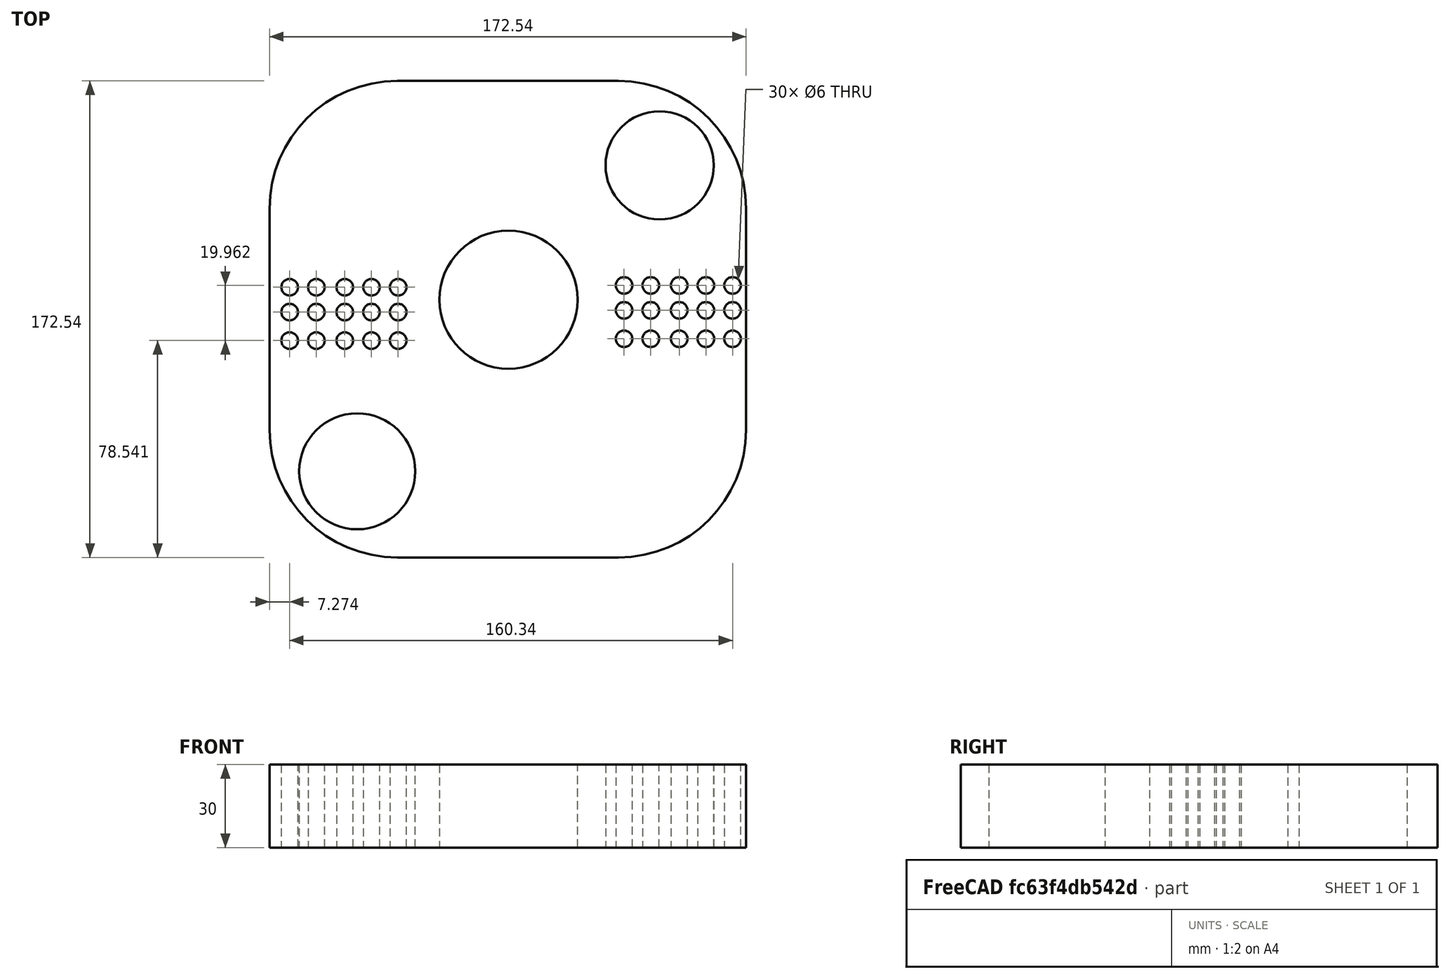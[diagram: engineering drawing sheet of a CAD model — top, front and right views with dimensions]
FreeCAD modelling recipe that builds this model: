
FCSTD DOCUMENT  (FreeCAD 0.18R16131 (Git))
Label: Momentum_Mold_Plate_1-2_160X200_12T_25mm(lm12uu) (2)
License: All rights reserved
LicenseURL: http://en.wikipedia.org/wiki/All_rights_reserved
objects: PartDesign::Pad×2, Sketcher::SketchObject×1, PartDesign::Body×1
note: 6 computed .brp shape members not serialized (recipe doc carries the construction recipe); baked Part::Feature solids carry a one-line shape summary decoded from their .brp

FEATURE [Sketcher::SketchObject] Sketch
  MapMode = 5
  Support = -> [XY_Plane]
  sketch-geometry (41):
    g0: LineSegment StartX=-35.5842 StartY=-63.1111 StartZ=0 EndX=44.4158 EndY=-63.1111 EndZ=0
    g1: LineSegment StartX=90.685 StartY=-16.8419 StartZ=0 EndX=90.685 EndY=63.1581 EndZ=0
    g2: LineSegment StartX=44.4158 StartY=109.427 StartZ=0 EndX=-35.5842 EndY=109.427 EndZ=0
    g3: LineSegment StartX=-81.8534 StartY=63.1581 StartZ=0 EndX=-81.8534 EndY=-16.8419 EndZ=0
    g4: Circle CenterX=4.62833 CenterY=30.2412 CenterZ=0 NormalX=0 NormalY=0 NormalZ=1 AngleXU=0 Radius=25
    g5: Circle CenterX=-50.1062 CenterY=-31.8986 CenterZ=0 NormalX=0 NormalY=0 NormalZ=1 AngleXU=0 Radius=21
    g6: Circle CenterX=59.3629 CenterY=78.8583 CenterZ=0 NormalX=0 NormalY=0 NormalZ=1 AngleXU=0 Radius=19.5845
    g7: ArcOfCircle CenterX=-35.5842 CenterY=63.1581 CenterZ=0 NormalX=0 NormalY=0 NormalZ=1 AngleXU=0 Radius=46.2692 StartAngle=1.5708 EndAngle=3.14159
    g8: ArcOfCircle CenterX=44.4158 CenterY=63.1581 CenterZ=0 NormalX=0 NormalY=0 NormalZ=1 AngleXU=0 Radius=46.2692 StartAngle=1e-16 EndAngle=1.5708
    g9: ArcOfCircle CenterX=44.4158 CenterY=-16.8419 CenterZ=0 NormalX=0 NormalY=0 NormalZ=1 AngleXU=0 Radius=46.2692 StartAngle=4.71239 EndAngle=6.28319
    g10: ArcOfCircle CenterX=-35.5842 CenterY=-16.8419 CenterZ=0 NormalX=0 NormalY=0 NormalZ=1 AngleXU=0 Radius=46.2692 StartAngle=3.14159 EndAngle=4.71239
    g11: Circle CenterX=-74.5758 CenterY=34.7487 CenterZ=0 NormalX=0 NormalY=0 NormalZ=1 AngleXU=0 Radius=3
    g12: Circle CenterX=-64.9167 CenterY=34.7487 CenterZ=0 NormalX=0 NormalY=0 NormalZ=1 AngleXU=0 Radius=3
    g13: Circle CenterX=-54.6138 CenterY=34.7487 CenterZ=0 NormalX=0 NormalY=0 NormalZ=1 AngleXU=0 Radius=3
    g14: Circle CenterX=-44.9547 CenterY=34.7487 CenterZ=0 NormalX=0 NormalY=0 NormalZ=1 AngleXU=0 Radius=3
    g15: Circle CenterX=-35.2957 CenterY=34.7487 CenterZ=0 NormalX=0 NormalY=0 NormalZ=1 AngleXU=0 Radius=3
    g16: Circle CenterX=-74.5758 CenterY=25.7336 CenterZ=0 NormalX=0 NormalY=0 NormalZ=1 AngleXU=0 Radius=3
    g17: Circle CenterX=-64.9167 CenterY=25.7336 CenterZ=0 NormalX=0 NormalY=0 NormalZ=1 AngleXU=0 Radius=3
    g18: Circle CenterX=-54.6138 CenterY=25.7336 CenterZ=0 NormalX=0 NormalY=0 NormalZ=1 AngleXU=0 Radius=3
    g19: Circle CenterX=-44.9547 CenterY=25.7336 CenterZ=0 NormalX=0 NormalY=0 NormalZ=1 AngleXU=0 Radius=3
    g20: Circle CenterX=-35.2957 CenterY=25.7336 CenterZ=0 NormalX=0 NormalY=0 NormalZ=1 AngleXU=0 Radius=3
    g21: Circle CenterX=-74.5758 CenterY=15.4306 CenterZ=0 NormalX=0 NormalY=0 NormalZ=1 AngleXU=0 Radius=3
    g22: Circle CenterX=-64.9167 CenterY=15.4306 CenterZ=0 NormalX=0 NormalY=0 NormalZ=1 AngleXU=0 Radius=3
    g23: Circle CenterX=-54.6138 CenterY=15.4306 CenterZ=0 NormalX=0 NormalY=0 NormalZ=1 AngleXU=0 Radius=3
    g24: Circle CenterX=-44.9547 CenterY=15.4306 CenterZ=0 NormalX=0 NormalY=0 NormalZ=1 AngleXU=0 Radius=3
    g25: Circle CenterX=-35.2957 CenterY=15.4306 CenterZ=0 NormalX=0 NormalY=0 NormalZ=1 AngleXU=0 Radius=3
    g26: Circle CenterX=46.4841 CenterY=35.3926 CenterZ=0 NormalX=0 NormalY=0 NormalZ=1 AngleXU=0 Radius=3
    g27: Circle CenterX=56.1432 CenterY=35.3926 CenterZ=0 NormalX=0 NormalY=0 NormalZ=1 AngleXU=0 Radius=3
    g28: Circle CenterX=66.4461 CenterY=35.3926 CenterZ=0 NormalX=0 NormalY=0 NormalZ=1 AngleXU=0 Radius=3
    g29: Circle CenterX=76.1052 CenterY=35.3926 CenterZ=0 NormalX=0 NormalY=0 NormalZ=1 AngleXU=0 Radius=3
    g30: Circle CenterX=85.7642 CenterY=35.3926 CenterZ=0 NormalX=0 NormalY=0 NormalZ=1 AngleXU=0 Radius=3
    g31: Circle CenterX=46.4841 CenterY=26.3775 CenterZ=0 NormalX=0 NormalY=0 NormalZ=1 AngleXU=0 Radius=3
    g32: Circle CenterX=56.1432 CenterY=26.3775 CenterZ=0 NormalX=0 NormalY=0 NormalZ=1 AngleXU=0 Radius=3
    g33: Circle CenterX=66.4461 CenterY=26.3775 CenterZ=0 NormalX=0 NormalY=0 NormalZ=1 AngleXU=0 Radius=3
    g34: Circle CenterX=76.1052 CenterY=26.3775 CenterZ=0 NormalX=0 NormalY=0 NormalZ=1 AngleXU=0 Radius=3
    g35: Circle CenterX=85.7642 CenterY=26.3775 CenterZ=0 NormalX=0 NormalY=0 NormalZ=1 AngleXU=0 Radius=3
    g36: Circle CenterX=46.4841 CenterY=16.0746 CenterZ=0 NormalX=0 NormalY=0 NormalZ=1 AngleXU=0 Radius=3
    g37: Circle CenterX=56.1432 CenterY=16.0746 CenterZ=0 NormalX=0 NormalY=0 NormalZ=1 AngleXU=0 Radius=3
    g38: Circle CenterX=66.4461 CenterY=16.0746 CenterZ=0 NormalX=0 NormalY=0 NormalZ=1 AngleXU=0 Radius=3
    g39: Circle CenterX=76.1052 CenterY=16.0746 CenterZ=0 NormalX=0 NormalY=0 NormalZ=1 AngleXU=0 Radius=3
    g40: Circle CenterX=85.7642 CenterY=16.0746 CenterZ=0 NormalX=0 NormalY=0 NormalZ=1 AngleXU=0 Radius=3
  constraints (63):
    c: Horizontal(g0)
    c: Horizontal(g2)
    c: Vertical(g1)
    c: Vertical(g3)
    c: Radius(g4) = 25
    c: Radius(g5) = 21
    c: Tangent(g2,g7) = -1.5708
    c: Tangent(g3,g7) = -1.5708
    c: Tangent(g2,g8) = -1.5708
    c: Tangent(g1,g8) = -1.5708
    c: Tangent(g1,g9) = -1.5708
    c: Tangent(g0,g9) = -1.5708
    c: Tangent(g0,g10) = -1.5708
    c: Tangent(g3,g10) = -1.5708
    c: Vertical(g7,g10)
    c: DistanceY(g1,g1) = 80
    c: DistanceY(g3,g3) = 80
    c: Horizontal(g1,g3)
    c: DistanceX(g2,g2) = 80
    c: Horizontal(g11,g12)
    c: Horizontal(g12,g13)
    c: Horizontal(g13,g14)
    c: Horizontal(g14,g15)
    c: Radius(g11) = 3
    c: Radius(g12) = 3
    c: Radius(g13) = 3
    c: Radius(g14) = 3
    c: Radius(g15) = 3
    c: Horizontal(g16,g17)
    c: Horizontal(g17,g18)
    c: Horizontal(g18,g19)
    c: Horizontal(g19,g20)
    c: Equal(g11,g16) = 3
    c: Equal(g12,g17) = 3
    c: Equal(g13,g18) = 3
    c: Equal(g14,g19) = 3
    c: Equal(g15,g20) = 3
    c: Horizontal(g21,g22)
    c: Horizontal(g22,g23)
    c: Horizontal(g23,g24)
    c: Horizontal(g24,g25)
    c: Horizontal(g26,g27)
    c: Horizontal(g27,g28)
    c: Horizontal(g28,g29)
    c: Horizontal(g29,g30)
    c: Equal(g11,g26) = 3
    c: Equal(g12,g27) = 3
    c: Equal(g13,g28) = 3
    c: Equal(g14,g29) = 3
    c: Equal(g15,g30) = 3
    c: Horizontal(g31,g32)
    c: Horizontal(g32,g33)
    c: Horizontal(g33,g34)
    c: Horizontal(g34,g35)
    c: Equal(g26,g31) = 3
    c: Equal(g27,g32) = 3
    c: Equal(g28,g33) = 3
    c: Equal(g29,g34) = 3
    c: Equal(g30,g35) = 3
    c: Horizontal(g36,g37)
    c: Horizontal(g37,g38)
    c: Horizontal(g38,g39)
    c: Horizontal(g39,g40)
FEATURE [PartDesign::Pad] Pad
  Length = 30
  Length2 = 100
  Profile = -> Sketch
  Type = 0
FEATURE [PartDesign::Pad] Pad001
  BaseFeature = -> Pad
  Length = 30
  Length2 = 100
  Profile = -> Sketch
  Type = 0
FEATURE [PartDesign::Body] Body
  Group = -> [Sketch,Pad,Pad001]
  Origin = -> Origin
  Tip = -> Pad001
